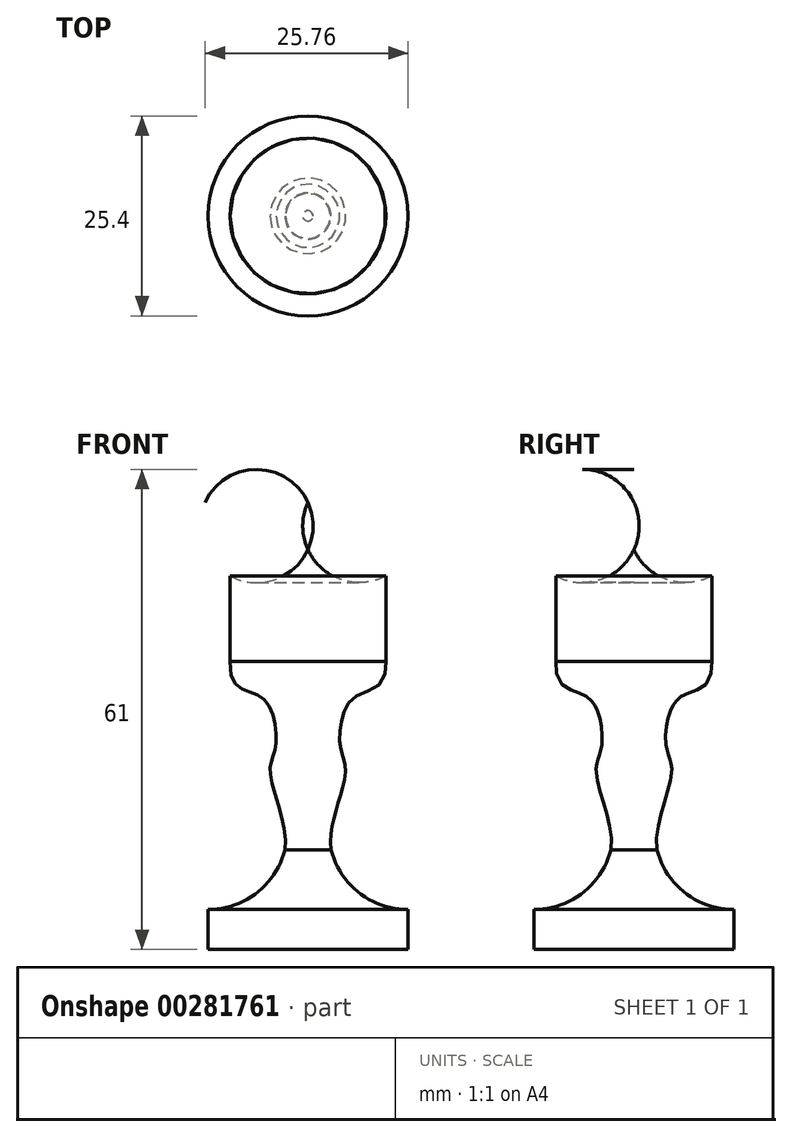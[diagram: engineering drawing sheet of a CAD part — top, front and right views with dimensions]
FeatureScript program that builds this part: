
annotation { "Feature Type Name" : "Feature", "Feature Type Description" : "" }
export const myFeature = defineFeature(function(context is Context, id is Id, definition is map)
    precondition{}
    {
        {
            var Q0;
            Q0=qCreatedBy(makeId("Right.planeOp"),FACE);
            var sketch = newSketch(context, id + "F0", { "sketchPlane" : qUnion([Q0])});
            skLineSegment(sketch, "E0", {"start": v(0, 0) * mm, "end": v(-12.7, 0) * mm});
            skLineSegment(sketch, "E1", {"start": v(-12.7, 0) * mm, "end": v(-12.7, 5.08) * mm});
            skLineSegment(sketch, "E2", {"start": v(0, 0) * mm, "end": v(0, 50.8) * mm});
            skArc(sketch, "E3", {"start": v(-12.7, 5.08) * mm, "mid": v(-6.52, 7.2) * mm, "end": v(-2.93, 12.66) * mm});
            skLineSegment(sketch, "E4", {"start": v(-12.7, 5.08) * mm, "end": v(-48.6, 5.08) * mm, "construction": true});
            skArc(sketch, "E5", {"start": v(-9.9, 47.46) * mm, "mid": v(-4.23, 47) * mm, "end": v(0, 50.8) * mm});
            skLineSegment(sketch, "E6", {"start": v(-9.9, 47.46) * mm, "end": v(-9.9, 36.6) * mm});
            skFitSpline(sketch, "E7", {"points": [v(-2.93, 12.66) * mm, v(-4.8, 22.5) * mm, v(-4.12, 25.73) * mm, v(-5.82, 32) * mm, v(-9.9, 36.6) * mm], "startDerivative": vector(4.79, 27.79) * mm, "endDerivative": vector(2.35, 49.77) * mm});
            skSolve(sketch);
        }
        {
            var Q0;
            Q0=makeQuery(id+"F0.imprint","IMPRINT",FACE,{"disambiguationData":[TD([[makeQuery(id+"F0.imprint","IMPRINT",EDGE,{"derivedFrom":sQuery(id+"F0.wireOp",EDGE,"E0")}),-1.0]])]});
            var Q1;
            Q1=sQuery(id+"F0.wireOp",EDGE,"E2");
            revolve(context, id + "F1", {"entities" : qUnion([Q0]), "axis" : qUnion([Q1]), "revolveType" : RevolveType.FULL});
        }
    });
